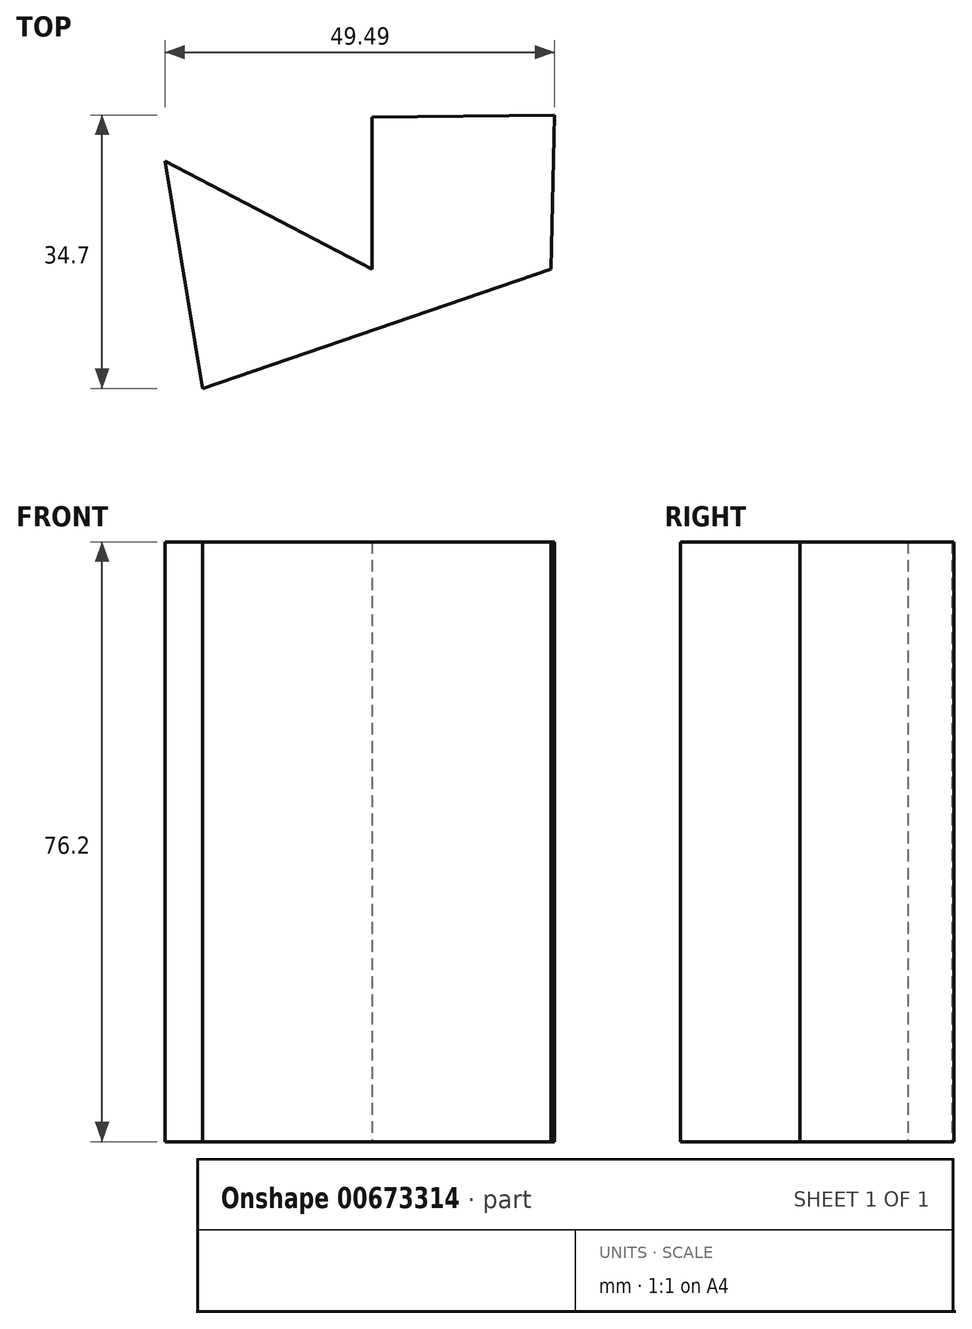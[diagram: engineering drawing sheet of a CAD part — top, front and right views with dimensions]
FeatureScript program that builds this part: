
annotation { "Feature Type Name" : "Feature", "Feature Type Description" : "" }
export const myFeature = defineFeature(function(context is Context, id is Id, definition is map)
    precondition{}
    {
        {
            var Q0;
            Q0=qCreatedBy(makeId("Top.planeOp"),FACE);
            var sketch = newSketch(context, id + "F0", { "sketchPlane" : qUnion([Q0])});
            skLineSegment(sketch, "E0", {"start": v(0, 0) * mm, "end": v(0, 19.3) * mm});
            skLineSegment(sketch, "E1", {"start": v(0, 19.3) * mm, "end": v(23.22, 19.55) * mm});
            skLineSegment(sketch, "E2", {"start": v(23.22, 19.55) * mm, "end": v(22.73, 0) * mm});
            skLineSegment(sketch, "E3", {"start": v(22.73, 0) * mm, "end": v(-21.5, -15.15) * mm});
            skLineSegment(sketch, "E4", {"start": v(-21.5, -15.15) * mm, "end": v(-26.27, 13.69) * mm});
            skLineSegment(sketch, "E5", {"start": v(-26.27, 13.69) * mm, "end": v(0, 0) * mm});
            skSolve(sketch);
        }
        {
            var Q0;
            Q0=makeQuery(id+"F0.imprint","IMPRINT",FACE,{"disambiguationData":[TD([[makeQuery(id+"F0.imprint","IMPRINT",EDGE,{"derivedFrom":sQuery(id+"F0.wireOp",EDGE,"E0")}),-1.0]])]});
            extrude(context, id + "F1", {"entities" : qUnion([Q0]), "depth" : 76.2 * mm, "offsetDistance" : 25.4 * mm});
        }
    });
